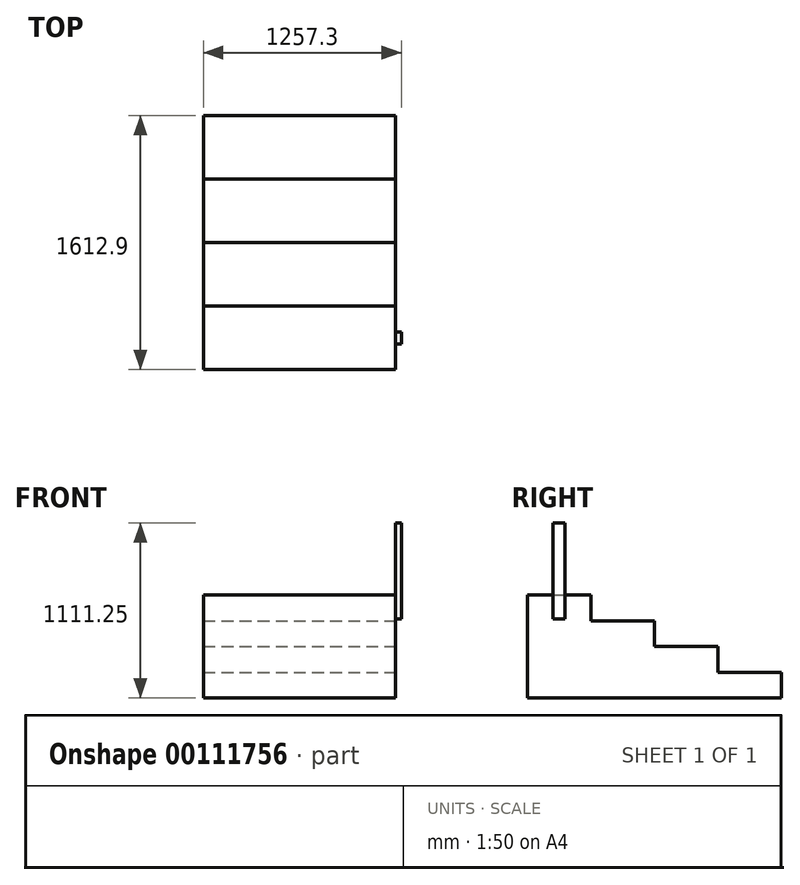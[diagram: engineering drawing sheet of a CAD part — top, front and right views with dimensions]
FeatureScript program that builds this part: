
annotation { "Feature Type Name" : "Feature", "Feature Type Description" : "" }
export const myFeature = defineFeature(function(context is Context, id is Id, definition is map)
    precondition{}
    {
        {
            var Q0;
            Q0=qCreatedBy(makeId("Right.planeOp"),FACE);
            var sketch = newSketch(context, id + "F0", { "sketchPlane" : qUnion([Q0])});
            skPoint(sketch, "E0.middle", {"position": v(0, 0) * mm});
            skLineSegment(sketch, "E1.bottom", {"start": v(-806.45, -327.03) * mm, "end": v(806.45, -327.03) * mm});
            skLineSegment(sketch, "E1.top", {"start": v(-806.45, 327.03) * mm, "end": v(-403.23, 327.03) * mm});
            skLineSegment(sketch, "E1.left", {"start": v(-806.45, -327.03) * mm, "end": v(-806.45, 327.03) * mm});
            skLineSegment(sketch, "E1.right", {"start": v(806.45, -327.03) * mm, "end": v(806.45, -163.51) * mm});
            skLineSegment(sketch, "E2", {"start": v(806.45, -163.51) * mm, "end": v(403.23, -163.51) * mm});
            skLineSegment(sketch, "E3", {"start": v(403.23, -163.51) * mm, "end": v(403.22, 0) * mm});
            skLineSegment(sketch, "E4", {"start": v(403.22, 0) * mm, "end": v(0, 0) * mm});
            skLineSegment(sketch, "E5", {"start": v(0, 0) * mm, "end": v(0, 163.51) * mm});
            skLineSegment(sketch, "E6", {"start": v(0, 163.51) * mm, "end": v(-403.23, 163.51) * mm});
            skLineSegment(sketch, "E7", {"start": v(-403.23, 163.51) * mm, "end": v(-403.23, 327.03) * mm});
            skLineSegment(sketch, "E8", {"start": v(-403.23, 327.03) * mm, "end": v(-806.45, 327.02) * mm});
            skPoint(sketch, "E9.orphan", {"position": v(806.45, 327.03) * mm});
            skSolve(sketch);
        }
        {
            var Q0;
            Q0=makeQuery(id+"F0.imprint","IMPRINT",FACE,{"disambiguationData":[TD([[makeQuery(id+"F0.imprint","IMPRINT",EDGE,{"derivedFrom":sQuery(id+"F0.wireOp",EDGE,"E1.bottom")}),1.0]])]});
            extrude(context, id + "F1", {"entities" : qUnion([Q0]), "oppositeDirection" : true, "depth" : 1219.2 * mm});
        }
        {
            var Q0;
            Q0=makeQuery(id+"F1.opExtrude","CAP_FACE",FACE,{"disambiguationData":[OSD([sQuery(id+"F0.wireOp",EDGE,"E1.bottom"),sQuery(id+"F0.wireOp",EDGE,"E1.left"),sQuery(id+"F0.wireOp",EDGE,"E1.right"),sQuery(id+"F0.wireOp",EDGE,"E2"),sQuery(id+"F0.wireOp",EDGE,"E3"),sQuery(id+"F0.wireOp",EDGE,"E4"),sQuery(id+"F0.wireOp",EDGE,"E5"),sQuery(id+"F0.wireOp",EDGE,"E6"),sQuery(id+"F0.wireOp",EDGE,"E7"),sQuery(id+"F0.wireOp",EDGE,"E8")])],"isStart":true});
            var sketch = newSketch(context, id + "F2", { "sketchPlane" : qUnion([Q0])});
            skLineSegment(sketch, "E10.bottom", {"start": v(-566.74, 174.62) * mm, "end": v(-642.94, 174.62) * mm});
            skLineSegment(sketch, "E10.top", {"start": v(-566.74, 784.22) * mm, "end": v(-642.94, 784.22) * mm});
            skLineSegment(sketch, "E10.left", {"start": v(-566.74, 174.62) * mm, "end": v(-566.74, 784.22) * mm});
            skLineSegment(sketch, "E10.right", {"start": v(-642.94, 174.63) * mm, "end": v(-642.94, 784.22) * mm});
            skPoint(sketch, "E10.middle", {"position": v(-604.84, 327.03) * mm});
            skSolve(sketch);
        }
        {
            var Q0;
            Q0 = qSketchRegion(id + "F2", true);
            extrude(context, id + "F3", {"entities" : qUnion([Q0]), "operationType" : NewBodyOperationType.ADD, "depth" : 38.1 * mm});
        }
    });
